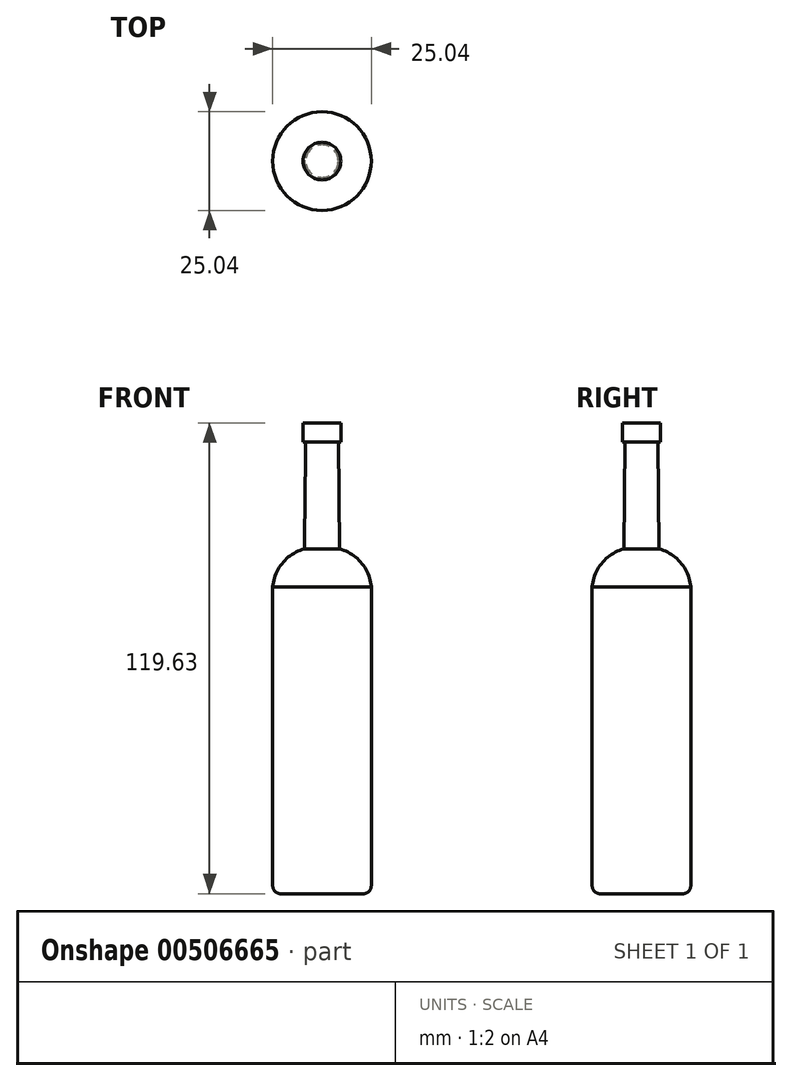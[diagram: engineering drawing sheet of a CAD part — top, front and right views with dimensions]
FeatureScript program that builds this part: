
annotation { "Feature Type Name" : "Feature", "Feature Type Description" : "" }
export const myFeature = defineFeature(function(context is Context, id is Id, definition is map)
    precondition{}
    {
        {
            var Q0;
            Q0=qCreatedBy(makeId("Front.planeOp"),FACE);
            var sketch = newSketch(context, id + "F0", { "sketchPlane" : qUnion([Q0])});
            skArc(sketch, "E0", {"start": v(12.52, 79.36) * mm, "mid": v(9.83, 85.68) * mm, "end": v(3.93, 89.18) * mm});
            skLineSegment(sketch, "E1", {"start": v(-4.54, 115.94) * mm, "end": v(-5.1, 115.95) * mm});
            skLineSegment(sketch, "E2", {"start": v(-5.01, 121.03) * mm, "end": v(4.78, 121.03) * mm});
            skLineSegment(sketch, "E3", {"start": v(4.78, 121.03) * mm, "end": v(4.78, 116.17) * mm});
            skLineSegment(sketch, "E4", {"start": v(4.78, 116.17) * mm, "end": v(4.14, 116.17) * mm});
            skLineSegment(sketch, "E5", {"start": v(4.14, 116.17) * mm, "end": v(4.46, 89.05) * mm});
            skPoint(sketch, "E5.endSnap0", {"position": v(4.46, 116.17) * mm});
            skLineSegment(sketch, "E6", {"start": v(12.52, 79.36) * mm, "end": v(12.52, 3.57) * mm});
            skLineSegment(sketch, "E7", {"start": v(10.33, 1.4) * mm, "end": v(0, 1.4) * mm});
            skLineSegment(sketch, "E8", {"start": v(-10.6, 1.4) * mm, "end": v(-11.3, 1.4) * mm});
            skLineSegment(sketch, "E9", {"start": v(-13.3, 3.4) * mm, "end": v(-13.3, 3.54) * mm});
            skLineSegment(sketch, "E10", {"start": v(10.33, 1.4) * mm, "end": v(10.52, 1.4) * mm});
            skLineSegment(sketch, "E11", {"start": v(12.52, 3.4) * mm, "end": v(12.52, 3.57) * mm});
            skPoint(sketch, "E12.visualSharp", {"position": v(12.52, 1.4) * mm});
            skArc(sketch, "E12.filletArc", {"start": v(10.52, 1.4) * mm, "mid": v(11.93, 1.99) * mm, "end": v(12.52, 3.4) * mm});
            skLineSegment(sketch, "E13", {"start": v(0, 1.4) * mm, "end": v(0, 121.03) * mm});
            skPoint(sketch, "E13.endSnap0", {"position": v(-0.11, 121.03) * mm});
            skSolve(sketch);
        }
        {
            var Q0;
            {var subQ3=sQuery(id+"F0.wireOp",EDGE,"E3");Q0=makeQuery(id+"F0.imprint","IMPRINT",FACE,{"disambiguationData":[TD([[makeQuery(id+"F0.imprint","IMPRINT",EDGE,{"derivedFrom":subQ3}),-1.0]])]});}
            var Q1;
            Q1=sQuery(id+"F0.wireOp",EDGE,"E13");
            revolve(context, id + "F1", {"entities" : qUnion([Q0]), "axis" : qUnion([Q1]), "revolveType" : RevolveType.FULL});
        }
    });
